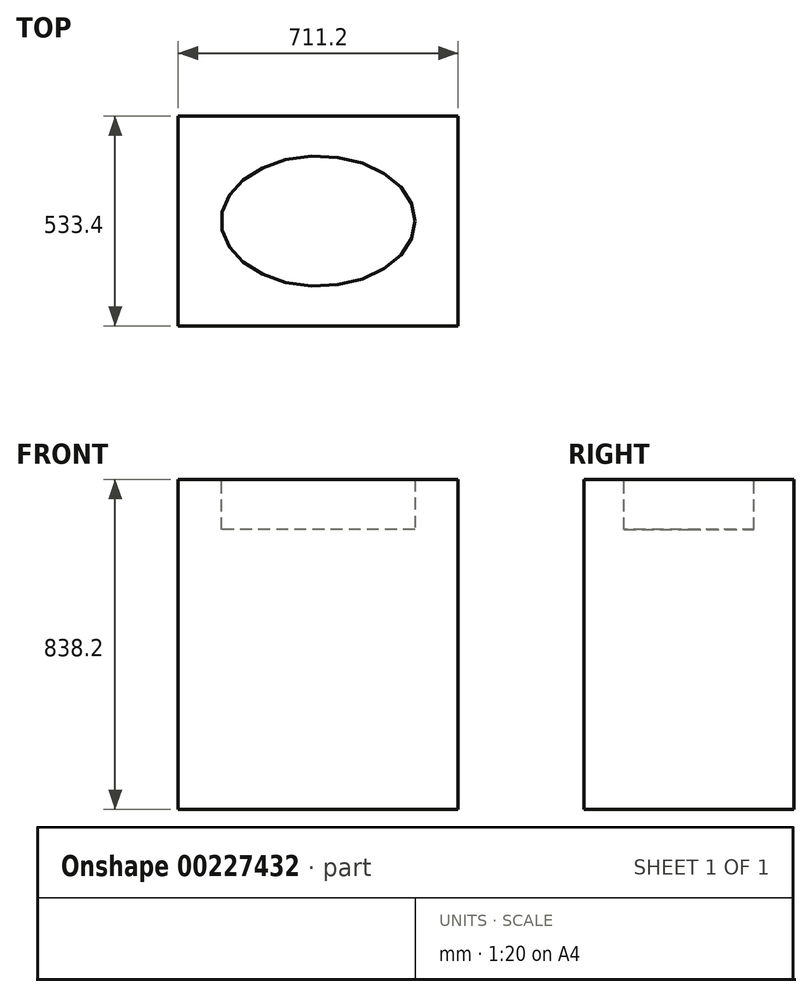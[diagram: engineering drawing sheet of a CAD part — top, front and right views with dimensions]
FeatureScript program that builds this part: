
annotation { "Feature Type Name" : "Feature", "Feature Type Description" : "" }
export const myFeature = defineFeature(function(context is Context, id is Id, definition is map)
    precondition{}
    {
        {
            var Q0;
            Q0=qCreatedBy(makeId("Top.planeOp"),FACE);
            var sketch = newSketch(context, id + "F0", { "sketchPlane" : qUnion([Q0])});
            skLineSegment(sketch, "E0.bottom", {"start": v(0, 0) * mm, "end": v(711.2, 0) * mm});
            skLineSegment(sketch, "E0.top", {"start": v(0, 533.4) * mm, "end": v(711.2, 533.4) * mm});
            skLineSegment(sketch, "E0.left", {"start": v(0, 0) * mm, "end": v(0, 533.4) * mm});
            skLineSegment(sketch, "E0.right", {"start": v(711.2, 0) * mm, "end": v(711.2, 533.4) * mm});
            skPoint(sketch, "E1", {"position": v(0, 266.7) * mm});
            skPoint(sketch, "E2", {"position": v(355.6, 533.4) * mm});
            skEllipse(sketch, "E3", {"center": v(355.6, 266.7) * mm, "majorRadius": 245.82 * mm, "minorRadius": 165.28 * mm, "majorAxis": v(1, 0)});
            skSolve(sketch);
        }
        {
            var Q0;
            Q0=makeQuery(id+"F0.imprint","IMPRINT",FACE,{"disambiguationData":[TD([[makeQuery(id+"F0.imprint","IMPRINT",EDGE,{"derivedFrom":sQuery(id+"F0.wireOp",EDGE,"E0.bottom")}),1.0]])]});
            extrude(context, id + "F1", {"entities" : qUnion([Q0]), "depth" : 838.2 * mm});
        }
        {
            var Q0;
            Q0=makeQuery(id+"F0.imprint","IMPRINT",FACE,{"disambiguationData":[TD([[makeQuery(id+"F0.imprint","IMPRINT",EDGE,{"derivedFrom":sQuery(id+"F0.wireOp",EDGE,"E3")}),1.0]])]});
            extrude(context, id + "F2", {"entities" : qUnion([Q0]), "operationType" : NewBodyOperationType.ADD, "depth" : 711.2 * mm});
        }
    });
